# Revit family: FA_КоробкаУравниванияПотенциалов_EZETEK
name_source: partatom
category: Системы пожарной сигнализации
revit_build: Autodesk Revit 2017 (Build: 20170118_1100(x64)
units: mm (PartAtom-declared; Revit-internal decimal feet)

## family parameters
Всегда вертикально = Да
На основе рабочей плоскости = Нет
Общий = Да
При загрузке вырезать с полостями = Нет
Размер круглого соединителя = Использовать радиус
Сохранять ориентацию аннотаций = Нет
Тип детали = Нормальный
Точка расчета площади = Нет

## types (2) — shared parameters
ADSK_Версия Revit = 2017
ADSK_Единица измерения = шт.
ADSK_Завод-изготовитель = Ezetek
ADSK_Количество = 1
ADSK_Материал = BIMLIB_Пластик_Серый_EZETEK
ADSK_Обозначение = 44457
URL = https://ezetek.ru
Группа модели = Коробки и шины уравнивания потенциалов
Изготовитель = Ezetek
Описание = Коробка уравнивания потенциалов предназначена для организации дополнительной системы уравнивания потенциалов в квартирах, домах, офисах и производственных помещениях — коробка объединяет защитные проводники электрического оборудования и подключается к ГЗШ. Коробка уравнивания потенциалов выполнена из пластика в герметичном исполнении со степенью защиты IP 55.
Угол = 90.00°

## per-type parameters (varying)
| type | ADSK_Код изделия | ADSK_Марка | ADSK_Масса | ADSK_Масса_Текст | ADSK_Наименование | Высота | Ширина |
| КоробкаУравниванияПотенциалов_85х85х40_44457 | 44457 | 44457 | 0.1 | 0.10 | Коробка уравнивания потенциалов 7 подключений 85х85х40 мм | 40 мм | 85 мм |
| КоробкаУравниванияПотенциалов_100х100х50_44458 | 44458 | 44458 | 0.14 | 0.14 | Коробка уравнивания потенциалов 13 подключений 100х100х50 мм | 50 мм | 100 мм |
